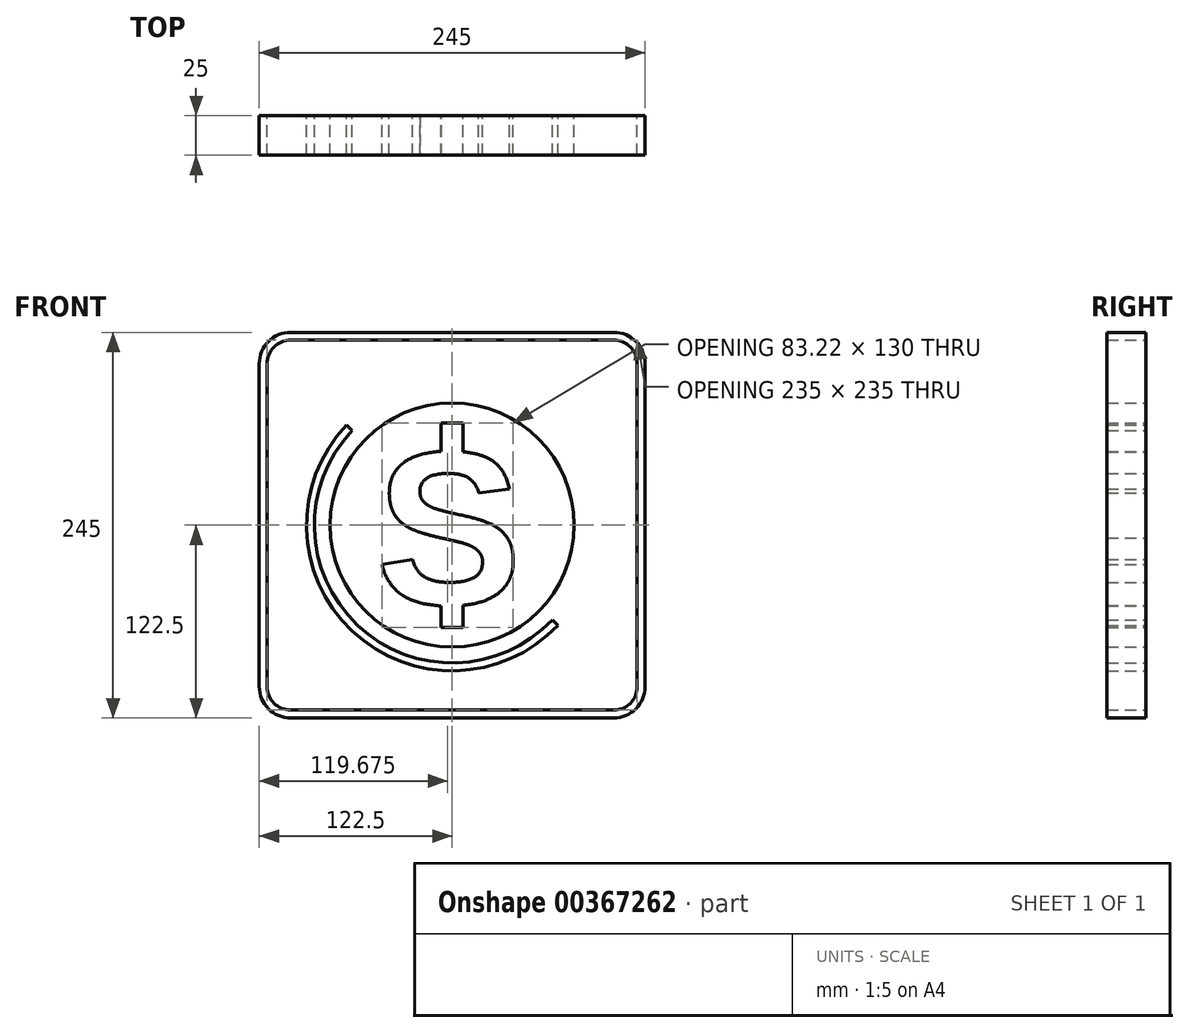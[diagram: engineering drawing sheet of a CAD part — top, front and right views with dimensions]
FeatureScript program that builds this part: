
annotation { "Feature Type Name" : "Feature", "Feature Type Description" : "" }
export const myFeature = defineFeature(function(context is Context, id is Id, definition is map)
    precondition{}
    {
        {
            var Q0;
            Q0=qCreatedBy(makeId("Front.planeOp"),FACE);
            var sketch = newSketch(context, id + "F0", { "sketchPlane" : qUnion([Q0])});
            skText(sketch, "E0", { "text": "S", "fontName": "Arimo-Bold.ttf"});
            skCircle(sketch, "E1", {"center": v(0, 0) * mm, "radius": 92.5 * mm});
            skLineSegment(sketch, "E2.bottom", {"start": v(-102.5, 117.5) * mm, "end": v(102.5, 117.5) * mm});
            skLineSegment(sketch, "E2.top", {"start": v(-102.5, -117.5) * mm, "end": v(102.5, -117.5) * mm});
            skLineSegment(sketch, "E2.left", {"start": v(-117.5, 102.5) * mm, "end": v(-117.5, -102.5) * mm});
            skLineSegment(sketch, "E2.right", {"start": v(117.5, 102.5) * mm, "end": v(117.5, -102.5) * mm});
            skLineSegment(sketch, "E3", {"start": v(-117.5, 117.5) * mm, "end": v(117.5, -117.5) * mm, "construction": true});
            skCircle(sketch, "E4.0", {"center": v(0, 0) * mm, "radius": 87.5 * mm});
            skPoint(sketch, "E5.visualSharp", {"position": v(-117.5, 117.5) * mm});
            skArc(sketch, "E5.filletArc", {"start": v(-102.5, 117.5) * mm, "mid": v(-113.1, 113.1) * mm, "end": v(-117.5, 102.5) * mm});
            skPoint(sketch, "E6.visualSharp", {"position": v(117.5, 117.5) * mm});
            skArc(sketch, "E6.filletArc", {"start": v(117.5, 102.5) * mm, "mid": v(113.1, 113.1) * mm, "end": v(102.5, 117.5) * mm});
            skPoint(sketch, "E7.visualSharp", {"position": v(117.5, -117.5) * mm});
            skArc(sketch, "E7.filletArc", {"start": v(102.5, -117.5) * mm, "mid": v(113.1, -113.1) * mm, "end": v(117.5, -102.5) * mm});
            skPoint(sketch, "E8.visualSharp", {"position": v(-117.5, -117.5) * mm});
            skArc(sketch, "E8.filletArc", {"start": v(-117.5, -102.5) * mm, "mid": v(-113.1, -113.1) * mm, "end": v(-102.5, -117.5) * mm});
            skLineSegment(sketch, "E9.bottom", {"start": v(-7, 65) * mm, "end": v(0, 65) * mm});
            skLineSegment(sketch, "E9.top", {"start": v(-7, 35) * mm, "end": v(0, 35) * mm});
            skLineSegment(sketch, "E9.left", {"start": v(-7, 65) * mm, "end": v(-7, 35) * mm});
            skLineSegment(sketch, "E9.right", {"start": v(0, 65) * mm, "end": v(0, 35) * mm, "construction": true});
            skLineSegment(sketch, "E10", {"start": v(-48.43, 0) * mm, "end": v(48.43, 0) * mm, "construction": true});
            skLineSegment(sketch, "E11.MirrorCS", {"start": v(7, 65) * mm, "end": v(0, 65) * mm});
            skLineSegment(sketch, "E12.MirrorCS", {"start": v(7, 65) * mm, "end": v(7, 35) * mm});
            skLineSegment(sketch, "E13.MirrorCS", {"start": v(7, -65) * mm, "end": v(7, -35) * mm});
            skLineSegment(sketch, "E14.MirrorCS", {"start": v(7, -65) * mm, "end": v(0, -65) * mm});
            skLineSegment(sketch, "E15.MirrorCS", {"start": v(-7, -65) * mm, "end": v(0, -65) * mm});
            skLineSegment(sketch, "E16.MirrorCS", {"start": v(-7, -65) * mm, "end": v(-7, -35) * mm});
            skArc(sketch, "E17.0", {"start": v(-102.5, 122.5) * mm, "mid": v(-116.64, 116.64) * mm, "end": v(-122.5, 102.5) * mm});
            skLineSegment(sketch, "E17.1", {"start": v(-102.5, 122.5) * mm, "end": v(102.5, 122.5) * mm});
            skLineSegment(sketch, "E17.2", {"start": v(-122.5, 102.5) * mm, "end": v(-122.5, -102.5) * mm});
            skArc(sketch, "E17.3", {"start": v(122.5, 102.5) * mm, "mid": v(116.64, 116.64) * mm, "end": v(102.5, 122.5) * mm});
            skArc(sketch, "E17.4", {"start": v(-122.5, -102.5) * mm, "mid": v(-116.64, -116.64) * mm, "end": v(-102.5, -122.5) * mm});
            skLineSegment(sketch, "E17.5", {"start": v(-102.5, -122.5) * mm, "end": v(102.5, -122.5) * mm});
            skArc(sketch, "E17.6", {"start": v(102.5, -122.5) * mm, "mid": v(116.64, -116.64) * mm, "end": v(122.5, -102.5) * mm});
            skLineSegment(sketch, "E17.7", {"start": v(122.5, 102.5) * mm, "end": v(122.5, -102.5) * mm});
            skLineSegment(sketch, "E18.0", {"start": v(-114.73, 111.2) * mm, "end": v(111.2, -114.73) * mm});
            skLineSegment(sketch, "E19.MirrorCS", {"start": v(-111.2, 114.73) * mm, "end": v(114.73, -111.2) * mm});
            skCircle(sketch, "E20.0", {"center": v(0, 0) * mm, "radius": 77.5 * mm});
            const initialGuessF0  = {"E0": [-0.04843, -0.05, 1, 0, 0.1]};
            skSetInitialGuess(sketch, initialGuessF0);
            skSolve(sketch);
        }
        {
            var Q0;
            {var subQ19=sQuery(id+"F0.wireOp",EDGE,"E0.sketch_text.stroke-3");Q0=makeQuery(id+"F0.imprint","IMPRINT",FACE,{"disambiguationData":[TD([[makeQuery(id+"F0.imprint","IMPRINT",EDGE,{"derivedFrom":subQ19}),1.0]])]});}
            var Q1;
            {var subQ11=sQuery(id+"F0.wireOp",EDGE,"E0.sketch_text.stroke-19");Q1=makeQuery(id+"F0.imprint","IMPRINT",FACE,{"disambiguationData":[TD([[makeQuery(id+"F0.imprint","IMPRINT",EDGE,{"derivedFrom":subQ11}),1.0]])]});}
            var Q2;
            {var subQ0=sQuery(id+"F0.wireOp",EDGE,"E18.0");var subQ1=sQuery(id+"F0.wireOp",EDGE,"E0.sketch_text.stroke-16");var subQ2=makeQuery(id+"F0.imprint","INTERSECT",VERTEX,{"derivedFrom":[subQ1,subQ0]});Q2=makeQuery(id+"F0.imprint","IMPRINT",FACE,{"disambiguationData":[TD([[makeQuery(id+"F0.imprint","IMPRINT",EDGE,{"disambiguationData":[TD([[subQ2,-1.0]])],"derivedFrom":subQ1}),1.0]])]});}
            var Q3;
            {var subQ0=sQuery(id+"F0.wireOp",EDGE,"E18.0");var subQ1=sQuery(id+"F0.wireOp",EDGE,"E1");var subQ2=makeQuery(id+"F0.imprint","INTERSECT",VERTEX,{"disambiguationData":[OD(0.0)],"derivedFrom":[subQ1,subQ0]});Q3=makeQuery(id+"F0.imprint","IMPRINT",FACE,{"disambiguationData":[TD([[makeQuery(id+"F0.imprint","IMPRINT",EDGE,{"disambiguationData":[TD([[subQ2,-1.0]])],"derivedFrom":subQ1}),1.0]])]});}
            var Q4;
            {var subQ0=sQuery(id+"F0.wireOp",EDGE,"E18.0");var subQ1=sQuery(id+"F0.wireOp",EDGE,"E1");var subQ2=makeQuery(id+"F0.imprint","INTERSECT",VERTEX,{"disambiguationData":[OD(0.0)],"derivedFrom":[subQ1,subQ0]});Q4=makeQuery(id+"F0.imprint","IMPRINT",FACE,{"disambiguationData":[TD([[makeQuery(id+"F0.imprint","IMPRINT",EDGE,{"disambiguationData":[TD([[subQ2,1.0]])],"derivedFrom":subQ1}),1.0]])]});}
            var Q5;
            {var subQ0=sQuery(id+"F0.wireOp",EDGE,"E19.MirrorCS");var subQ1=sQuery(id+"F0.wireOp",EDGE,"E1");var subQ2=makeQuery(id+"F0.imprint","INTERSECT",VERTEX,{"disambiguationData":[OD(0.0)],"derivedFrom":[subQ1,subQ0]});Q5=makeQuery(id+"F0.imprint","IMPRINT",FACE,{"disambiguationData":[TD([[makeQuery(id+"F0.imprint","IMPRINT",EDGE,{"disambiguationData":[TD([[subQ2,1.0]])],"derivedFrom":subQ1}),1.0]])]});}
            var Q6;
            {var subQ6=sQuery(id+"F0.wireOp",EDGE,"E2.bottom");Q6=makeQuery(id+"F0.imprint","IMPRINT",FACE,{"disambiguationData":[TD([[makeQuery(id+"F0.imprint","IMPRINT",EDGE,{"derivedFrom":subQ6}),1.0]])]});}
            var Q7;
            {var subQ0=sQuery(id+"F0.wireOp",EDGE,"E18.0");var subQ1=sQuery(id+"F0.wireOp",EDGE,"E1");var subQ2=makeQuery(id+"F0.imprint","INTERSECT",VERTEX,{"disambiguationData":[OD(1.0)],"derivedFrom":[subQ1,subQ0]});Q7=makeQuery(id+"F0.imprint","IMPRINT",FACE,{"disambiguationData":[TD([[makeQuery(id+"F0.imprint","IMPRINT",EDGE,{"disambiguationData":[TD([[subQ2,-1.0]])],"derivedFrom":subQ1}),1.0]])]});}
            var Q8;
            {var subQ0=sQuery(id+"F0.wireOp",EDGE,"E0.sketch_text.stroke-9");Q8=makeQuery(id+"F0.imprint","IMPRINT",FACE,{"disambiguationData":[TD([[makeQuery(id+"F0.imprint","IMPRINT",EDGE,{"derivedFrom":subQ0}),1.0]])]});}
            var Q9;
            {var subQ4=sQuery(id+"F0.wireOp",EDGE,"E0.sketch_text.stroke-24");Q9=makeQuery(id+"F0.imprint","IMPRINT",FACE,{"disambiguationData":[TD([[makeQuery(id+"F0.imprint","IMPRINT",EDGE,{"derivedFrom":subQ4}),1.0]])]});}
            var Q10;
            {var subQ0=sQuery(id+"F0.wireOp",EDGE,"E19.MirrorCS");var subQ1=sQuery(id+"F0.wireOp",EDGE,"E0.sketch_text.stroke-0");var subQ2=makeQuery(id+"F0.imprint","INTERSECT",VERTEX,{"derivedFrom":[subQ1,subQ0]});Q10=makeQuery(id+"F0.imprint","IMPRINT",FACE,{"disambiguationData":[TD([[makeQuery(id+"F0.imprint","IMPRINT",EDGE,{"disambiguationData":[TD([[subQ2,-1.0]])],"derivedFrom":subQ1}),1.0]])]});}
            extrude(context, id + "F1", {"entities" : qUnion([Q0, Q1, Q2, Q3, Q4, Q5, Q6, Q7, Q8, Q9, Q10]), "depth" : 25 * mm});
        }
    });
